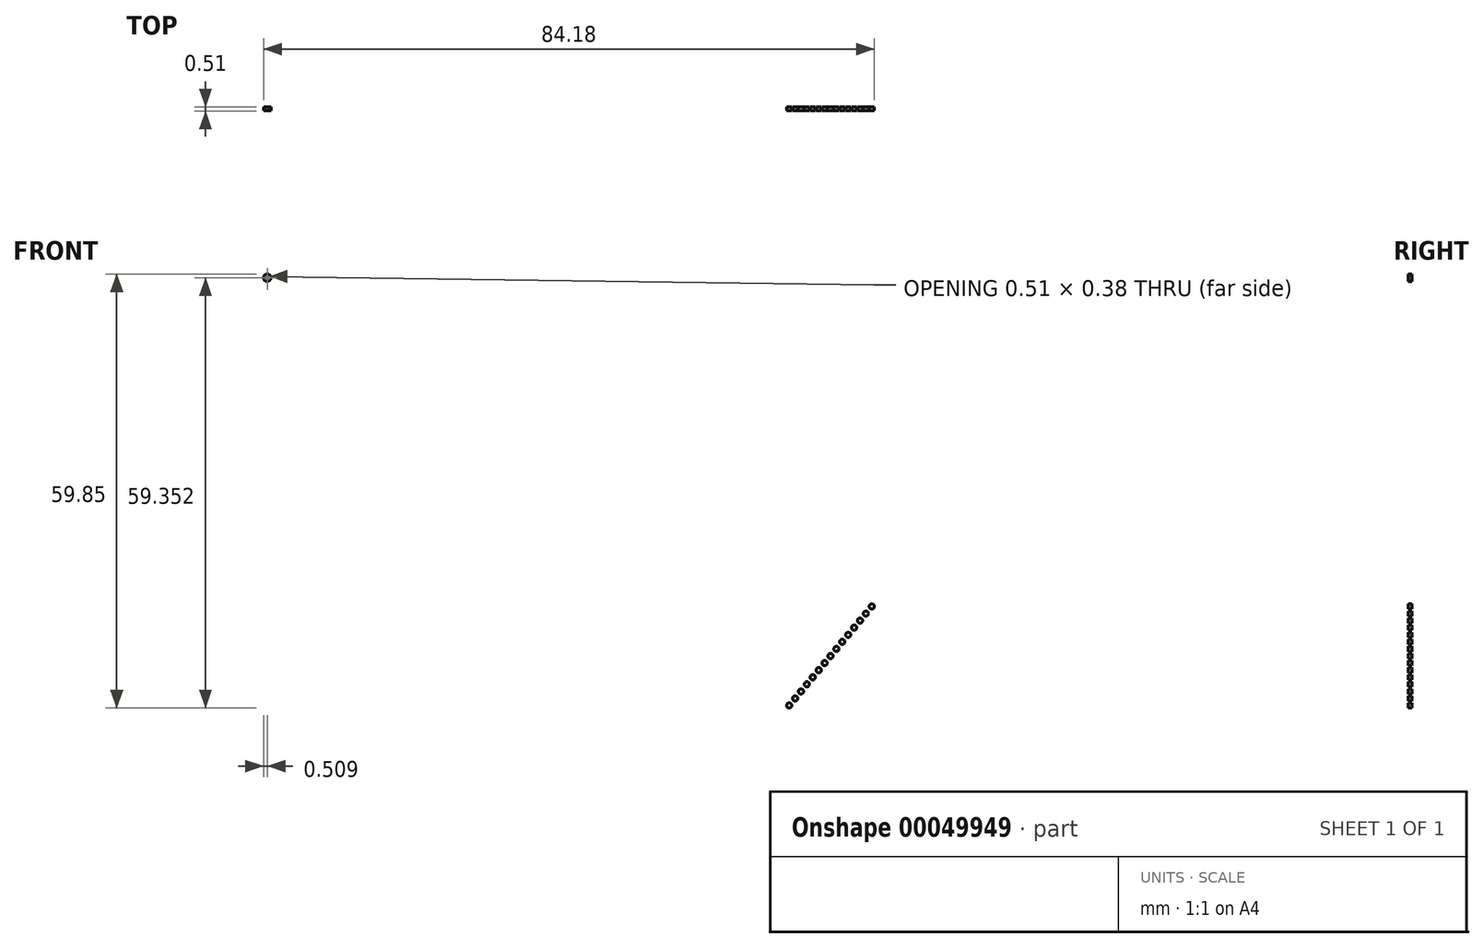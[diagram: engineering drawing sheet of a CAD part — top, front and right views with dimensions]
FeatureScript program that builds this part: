
annotation { "Feature Type Name" : "Feature", "Feature Type Description" : "" }
export const myFeature = defineFeature(function(context is Context, id is Id, definition is map)
    precondition{}
    {
        {
            var Q0;
            Q0=qCreatedBy(makeId("Front.planeOp"),FACE);
            var sketch = newSketch(context, id + "F0", { "sketchPlane" : qUnion([Q0])});
            skCircle(sketch, "E0", {"center": v(-69.08, 60.75) * mm, "radius": 0.5 * mm});
            skLineSegment(sketch, "E1", {"start": v(-69.59, 60.75) * mm, "end": v(-69.59, 55.67) * mm, "construction": true});
            skLineSegment(sketch, "E2", {"start": v(-69.08, 60.24) * mm, "end": v(-74.16, 60.24) * mm, "construction": true});
            skLineSegment(sketch, "E3", {"start": v(-69.33, 60.75) * mm, "end": v(-69.33, 60.57) * mm});
            skLineSegment(sketch, "E4", {"start": v(-68.83, 60.75) * mm, "end": v(-68.83, 60.57) * mm});
            skLineSegment(sketch, "E5", {"start": v(-69.33, 60.75) * mm, "end": v(-69.33, 60.95) * mm});
            skLineSegment(sketch, "E6", {"start": v(-69.33, 60.57) * mm, "end": v(-69.23, 60.57) * mm});
            skLineSegment(sketch, "E7", {"start": v(-69.23, 60.57) * mm, "end": v(-69.23, 60.84) * mm});
            skLineSegment(sketch, "E8", {"start": v(-69.08, 60.75) * mm, "end": v(-69.08, 60.69) * mm});
            skLineSegment(sketch, "E9", {"start": v(-68.83, 60.57) * mm, "end": v(-68.93, 60.57) * mm});
            skLineSegment(sketch, "E10", {"start": v(-68.93, 60.57) * mm, "end": v(-68.93, 60.84) * mm});
            skLineSegment(sketch, "E11", {"start": v(-69.08, 60.75) * mm, "end": v(-69.08, 60.24) * mm});
            skLineSegment(sketch, "E12", {"start": v(-69.08, 60.75) * mm, "end": v(-69.08, 61.26) * mm});
            skLineSegment(sketch, "E13", {"start": v(-69.33, 60.95) * mm, "end": v(-69.23, 60.95) * mm});
            skLineSegment(sketch, "E14", {"start": v(-69.23, 60.95) * mm, "end": v(-69.23, 60.93) * mm});
            skLineSegment(sketch, "E15", {"start": v(-69.08, 60.7) * mm, "end": v(-68.93, 60.7) * mm, "construction": true});
            skLineSegment(sketch, "E16", {"start": v(-69.08, 60.66) * mm, "end": v(-69.23, 60.66) * mm, "construction": true});
            skLineSegment(sketch, "E17", {"start": v(-69.08, 60.75) * mm, "end": v(-69.08, 60.57) * mm});
            skLineSegment(sketch, "E18", {"start": v(-69.08, 60.57) * mm, "end": v(-69.13, 60.57) * mm});
            skLineSegment(sketch, "E19", {"start": v(-69.08, 60.57) * mm, "end": v(-69.03, 60.57) * mm});
            skLineSegment(sketch, "E20", {"start": v(-69.13, 60.57) * mm, "end": v(-69.13, 60.84) * mm});
            skLineSegment(sketch, "E21", {"start": v(-69.03, 60.57) * mm, "end": v(-69.03, 60.84) * mm});
            skLineSegment(sketch, "E22", {"start": v(-69.23, 60.84) * mm, "end": v(-69.13, 60.84) * mm, "construction": true});
            skLineSegment(sketch, "E23", {"start": v(-69.03, 60.84) * mm, "end": v(-68.93, 60.84) * mm, "construction": true});
            skLineSegment(sketch, "E24", {"start": v(-69.18, 60.84) * mm, "end": v(-69.18, 60.86) * mm});
            skLineSegment(sketch, "E25", {"start": v(-68.98, 60.84) * mm, "end": v(-68.98, 60.86) * mm});
            skArc(sketch, "E26", {"start": v(-69.13, 60.84) * mm, "mid": v(-69.18, 60.86) * mm, "end": v(-69.23, 60.84) * mm});
            skArc(sketch, "E27", {"start": v(-68.93, 60.84) * mm, "mid": v(-68.98, 60.86) * mm, "end": v(-69.03, 60.84) * mm});
            skLineSegment(sketch, "E28", {"start": v(-69.23, 60.93) * mm, "end": v(-68.83, 60.93) * mm, "construction": true});
            skLineSegment(sketch, "E29", {"start": v(-69.23, 60.93) * mm, "end": v(-69.08, 60.93) * mm});
            skLineSegment(sketch, "E30", {"start": v(-69.16, 60.93) * mm, "end": v(-69.16, 60.95) * mm});
            skArc(sketch, "E31", {"start": v(-69.08, 60.93) * mm, "mid": v(-69.16, 60.95) * mm, "end": v(-69.23, 60.93) * mm});
            skLineSegment(sketch, "E32", {"start": v(-68.93, 60.84) * mm, "end": v(-68.93, 60.93) * mm, "construction": true});
            skLineSegment(sketch, "E33", {"start": v(-69.08, 60.93) * mm, "end": v(-68.93, 60.93) * mm});
            skLineSegment(sketch, "E34", {"start": v(-69, 60.93) * mm, "end": v(-69, 60.95) * mm});
            skArc(sketch, "E35", {"start": v(-68.93, 60.93) * mm, "mid": v(-69, 60.95) * mm, "end": v(-69.08, 60.93) * mm});
            skLineSegment(sketch, "E36", {"start": v(-68.85, 60.93) * mm, "end": v(-68.83, 60.9) * mm});
            skLineSegment(sketch, "E37", {"start": v(-68.84, 60.91) * mm, "end": v(-68.84, 60.92) * mm});
            skArc(sketch, "E38", {"start": v(-68.83, 60.9) * mm, "mid": v(-68.84, 60.92) * mm, "end": v(-68.85, 60.93) * mm});
            skLineSegment(sketch, "E39", {"start": v(-68.93, 60.93) * mm, "end": v(-68.85, 60.93) * mm});
            skLineSegment(sketch, "E40", {"start": v(-68.83, 60.9) * mm, "end": v(-68.83, 60.75) * mm});
            skLineSegment(sketch, "E41", {"start": v(15.33, 16.73) * mm, "end": v(2.62, 1.49) * mm});
            skCircle(sketch, "E42", {"center": v(2.85, 1.76) * mm, "radius": 0.36 * mm});
            skLineSegment(sketch, "E43", {"start": v(2.85, 1.76) * mm, "end": v(2.58, 1.99) * mm});
            skLineSegment(sketch, "E44", {"start": v(2.58, 1.99) * mm, "end": v(3.4, 2.96) * mm, "construction": true});
            skLineSegment(sketch, "E45", {"start": v(3.4, 2.96) * mm, "end": v(3.67, 2.74) * mm});
            skCircle(sketch, "E46", {"center": v(3.67, 2.74) * mm, "radius": 0.36 * mm});
            skLineSegment(sketch, "E47", {"start": v(3.4, 2.96) * mm, "end": v(4.2, 3.94) * mm, "construction": true});
            skLineSegment(sketch, "E48", {"start": v(4.2, 3.94) * mm, "end": v(4.48, 3.71) * mm});
            skCircle(sketch, "E49", {"center": v(4.48, 3.71) * mm, "radius": 0.36 * mm});
            skLineSegment(sketch, "E50", {"start": v(4.2, 3.94) * mm, "end": v(5.02, 4.92) * mm, "construction": true});
            skLineSegment(sketch, "E51", {"start": v(5.02, 4.92) * mm, "end": v(5.3, 4.69) * mm});
            skCircle(sketch, "E52", {"center": v(5.3, 4.69) * mm, "radius": 0.36 * mm});
            skLineSegment(sketch, "E53", {"start": v(5.02, 4.92) * mm, "end": v(5.83, 5.9) * mm, "construction": true});
            skLineSegment(sketch, "E54", {"start": v(5.83, 5.9) * mm, "end": v(6.1, 5.66) * mm});
            skCircle(sketch, "E55", {"center": v(6.1, 5.66) * mm, "radius": 0.36 * mm});
            skLineSegment(sketch, "E56", {"start": v(5.83, 5.9) * mm, "end": v(6.64, 6.87) * mm, "construction": true});
            skLineSegment(sketch, "E57", {"start": v(6.64, 6.87) * mm, "end": v(6.92, 6.64) * mm});
            skCircle(sketch, "E58", {"center": v(6.92, 6.64) * mm, "radius": 0.36 * mm});
            skLineSegment(sketch, "E59", {"start": v(6.64, 6.87) * mm, "end": v(7.46, 7.84) * mm, "construction": true});
            skLineSegment(sketch, "E60", {"start": v(7.46, 7.84) * mm, "end": v(7.73, 7.61) * mm});
            skCircle(sketch, "E61", {"center": v(7.73, 7.61) * mm, "radius": 0.36 * mm});
            skLineSegment(sketch, "E62", {"start": v(7.46, 7.84) * mm, "end": v(8.27, 8.82) * mm, "construction": true});
            skLineSegment(sketch, "E63", {"start": v(8.27, 8.82) * mm, "end": v(8.54, 8.6) * mm});
            skCircle(sketch, "E64", {"center": v(8.54, 8.6) * mm, "radius": 0.36 * mm});
            skLineSegment(sketch, "E65", {"start": v(8.27, 8.82) * mm, "end": v(9.08, 9.8) * mm, "construction": true});
            skLineSegment(sketch, "E66", {"start": v(9.08, 9.8) * mm, "end": v(9.36, 9.57) * mm});
            skCircle(sketch, "E67", {"center": v(9.36, 9.57) * mm, "radius": 0.36 * mm});
            skLineSegment(sketch, "E68", {"start": v(9.08, 9.8) * mm, "end": v(9.9, 10.77) * mm, "construction": true});
            skLineSegment(sketch, "E69", {"start": v(9.9, 10.77) * mm, "end": v(10.17, 10.54) * mm});
            skCircle(sketch, "E70", {"center": v(10.17, 10.54) * mm, "radius": 0.36 * mm});
            skLineSegment(sketch, "E71", {"start": v(9.9, 10.77) * mm, "end": v(10.7, 11.74) * mm, "construction": true});
            skLineSegment(sketch, "E72", {"start": v(10.7, 11.74) * mm, "end": v(10.98, 11.52) * mm});
            skLineSegment(sketch, "E73", {"start": v(10.7, 11.74) * mm, "end": v(11.52, 12.72) * mm, "construction": true});
            skLineSegment(sketch, "E74", {"start": v(11.52, 12.72) * mm, "end": v(11.8, 12.5) * mm, "construction": true});
            skLineSegment(sketch, "E75", {"start": v(11.52, 12.72) * mm, "end": v(12.34, 13.7) * mm, "construction": true});
            skLineSegment(sketch, "E76", {"start": v(12.34, 13.7) * mm, "end": v(12.6, 13.47) * mm});
            skLineSegment(sketch, "E77", {"start": v(12.34, 13.7) * mm, "end": v(13.15, 14.67) * mm, "construction": true});
            skLineSegment(sketch, "E78", {"start": v(13.15, 14.67) * mm, "end": v(13.42, 14.44) * mm});
            skLineSegment(sketch, "E79", {"start": v(13.15, 14.67) * mm, "end": v(13.96, 15.65) * mm, "construction": true});
            skLineSegment(sketch, "E80", {"start": v(13.96, 15.65) * mm, "end": v(14.23, 15.42) * mm});
            skLineSegment(sketch, "E81", {"start": v(13.96, 15.65) * mm, "end": v(14.77, 16.62) * mm, "construction": true});
            skLineSegment(sketch, "E82", {"start": v(14.77, 16.62) * mm, "end": v(15.05, 16.4) * mm, "construction": true});
            skCircle(sketch, "E83", {"center": v(10.98, 11.52) * mm, "radius": 0.36 * mm});
            skCircle(sketch, "E84", {"center": v(11.8, 12.5) * mm, "radius": 0.36 * mm});
            skCircle(sketch, "E85", {"center": v(13.42, 14.44) * mm, "radius": 0.36 * mm});
            skCircle(sketch, "E86", {"center": v(12.6, 13.47) * mm, "radius": 0.36 * mm});
            skCircle(sketch, "E87", {"center": v(14.23, 15.42) * mm, "radius": 0.36 * mm});
            skCircle(sketch, "E88", {"center": v(15.05, 16.4) * mm, "radius": 0.36 * mm});
            skSolve(sketch);
        }
        {
            var Q0;
            Q0=makeQuery(id+"F0.imprint","IMPRINT",FACE,{"disambiguationData":[TD([[makeQuery(id+"F0.imprint","IMPRINT",EDGE,{"derivedFrom":sQuery(id+"F0.wireOp",EDGE,"E3")}),-1.0]])]});
            var Q1;
            Q1=makeQuery(id+"F0.imprint","IMPRINT",FACE,{"disambiguationData":[TD([[makeQuery(id+"F0.imprint","IMPRINT",EDGE,{"derivedFrom":sQuery(id+"F0.wireOp",EDGE,"E4")}),1.0]])]});
            var Q2;
            {var subQ0=sQuery(id+"F0.wireOp",EDGE,"E41");var subQ1=makeQuery(id+"F0.imprint","INTERSECT",VERTEX,{"derivedFrom":[subQ0,sQuery(id+"F0.wireOp",EDGE,"E72")]});Q2=makeQuery(id+"F0.imprint","IMPRINT",FACE,{"disambiguationData":[TD([[makeQuery(id+"F0.imprint","IMPRINT",EDGE,{"disambiguationData":[TD([[subQ1,1.0]])],"derivedFrom":subQ0}),1.0]])]});}
            var Q3;
            {var subQ0=sQuery(id+"F0.wireOp",EDGE,"E41");var subQ1=makeQuery(id+"F0.imprint","INTERSECT",VERTEX,{"derivedFrom":[subQ0,sQuery(id+"F0.wireOp",EDGE,"E69")]});Q3=makeQuery(id+"F0.imprint","IMPRINT",FACE,{"disambiguationData":[TD([[makeQuery(id+"F0.imprint","IMPRINT",EDGE,{"disambiguationData":[TD([[subQ1,1.0]])],"derivedFrom":subQ0}),1.0]])]});}
            var Q4;
            {var subQ0=sQuery(id+"F0.wireOp",EDGE,"E60");Q4=makeQuery(id+"F0.imprint","IMPRINT",FACE,{"disambiguationData":[TD([[makeQuery(id+"F0.imprint","IMPRINT",EDGE,{"derivedFrom":subQ0}),1.0]])]});}
            var Q5;
            {var subQ0=sQuery(id+"F0.wireOp",EDGE,"E63");Q5=makeQuery(id+"F0.imprint","IMPRINT",FACE,{"disambiguationData":[TD([[makeQuery(id+"F0.imprint","IMPRINT",EDGE,{"derivedFrom":subQ0}),-1.0]])]});}
            var Q6;
            {var subQ0=sQuery(id+"F0.wireOp",EDGE,"E41");var subQ1=makeQuery(id+"F0.imprint","INTERSECT",VERTEX,{"derivedFrom":[subQ0,sQuery(id+"F0.wireOp",EDGE,"E43")]});Q6=makeQuery(id+"F0.imprint","IMPRINT",FACE,{"disambiguationData":[TD([[makeQuery(id+"F0.imprint","IMPRINT",EDGE,{"disambiguationData":[TD([[subQ1,1.0]])],"derivedFrom":subQ0}),1.0]])]});}
            var Q7;
            {var subQ0=sQuery(id+"F0.wireOp",EDGE,"E60");Q7=makeQuery(id+"F0.imprint","IMPRINT",FACE,{"disambiguationData":[TD([[makeQuery(id+"F0.imprint","IMPRINT",EDGE,{"derivedFrom":subQ0}),-1.0]])]});}
            var Q8;
            {var subQ0=sQuery(id+"F0.wireOp",EDGE,"E54");Q8=makeQuery(id+"F0.imprint","IMPRINT",FACE,{"disambiguationData":[TD([[makeQuery(id+"F0.imprint","IMPRINT",EDGE,{"derivedFrom":subQ0}),-1.0]])]});}
            var Q9;
            {var subQ0=sQuery(id+"F0.wireOp",EDGE,"E69");Q9=makeQuery(id+"F0.imprint","IMPRINT",FACE,{"disambiguationData":[TD([[makeQuery(id+"F0.imprint","IMPRINT",EDGE,{"derivedFrom":subQ0}),1.0]])]});}
            var Q10;
            {var subQ0=sQuery(id+"F0.wireOp",EDGE,"E63");Q10=makeQuery(id+"F0.imprint","IMPRINT",FACE,{"disambiguationData":[TD([[makeQuery(id+"F0.imprint","IMPRINT",EDGE,{"derivedFrom":subQ0}),1.0]])]});}
            var Q11;
            {var subQ0=sQuery(id+"F0.wireOp",EDGE,"E48");Q11=makeQuery(id+"F0.imprint","IMPRINT",FACE,{"disambiguationData":[TD([[makeQuery(id+"F0.imprint","IMPRINT",EDGE,{"derivedFrom":subQ0}),-1.0]])]});}
            var Q12;
            {var subQ3=sQuery(id+"F0.wireOp",EDGE,"E43");Q12=makeQuery(id+"F0.imprint","IMPRINT",FACE,{"disambiguationData":[TD([[makeQuery(id+"F0.imprint","IMPRINT",EDGE,{"derivedFrom":subQ3}),1.0]])]});}
            var Q13;
            {var subQ0=sQuery(id+"F0.wireOp",EDGE,"E57");Q13=makeQuery(id+"F0.imprint","IMPRINT",FACE,{"disambiguationData":[TD([[makeQuery(id+"F0.imprint","IMPRINT",EDGE,{"derivedFrom":subQ0}),1.0]])]});}
            var Q14;
            {var subQ0=sQuery(id+"F0.wireOp",EDGE,"E51");Q14=makeQuery(id+"F0.imprint","IMPRINT",FACE,{"disambiguationData":[TD([[makeQuery(id+"F0.imprint","IMPRINT",EDGE,{"derivedFrom":subQ0}),-1.0]])]});}
            var Q15;
            {var subQ0=sQuery(id+"F0.wireOp",EDGE,"E41");var subQ1=makeQuery(id+"F0.imprint","INTERSECT",VERTEX,{"derivedFrom":[subQ0,sQuery(id+"F0.wireOp",EDGE,"E45")]});Q15=makeQuery(id+"F0.imprint","IMPRINT",FACE,{"disambiguationData":[TD([[makeQuery(id+"F0.imprint","IMPRINT",EDGE,{"disambiguationData":[TD([[subQ1,1.0]])],"derivedFrom":subQ0}),1.0]])]});}
            var Q16;
            {var subQ0=sQuery(id+"F0.wireOp",EDGE,"E48");Q16=makeQuery(id+"F0.imprint","IMPRINT",FACE,{"disambiguationData":[TD([[makeQuery(id+"F0.imprint","IMPRINT",EDGE,{"derivedFrom":subQ0}),1.0]])]});}
            var Q17;
            {var subQ0=sQuery(id+"F0.wireOp",EDGE,"E57");Q17=makeQuery(id+"F0.imprint","IMPRINT",FACE,{"disambiguationData":[TD([[makeQuery(id+"F0.imprint","IMPRINT",EDGE,{"derivedFrom":subQ0}),-1.0]])]});}
            var Q18;
            {var subQ0=sQuery(id+"F0.wireOp",EDGE,"E41");var subQ1=makeQuery(id+"F0.imprint","INTERSECT",VERTEX,{"derivedFrom":[subQ0,sQuery(id+"F0.wireOp",EDGE,"E48")]});Q18=makeQuery(id+"F0.imprint","IMPRINT",FACE,{"disambiguationData":[TD([[makeQuery(id+"F0.imprint","IMPRINT",EDGE,{"disambiguationData":[TD([[subQ1,1.0]])],"derivedFrom":subQ0}),1.0]])]});}
            var Q19;
            {var subQ0=sQuery(id+"F0.wireOp",EDGE,"E41");var subQ1=makeQuery(id+"F0.imprint","INTERSECT",VERTEX,{"derivedFrom":[subQ0,sQuery(id+"F0.wireOp",EDGE,"E63")]});Q19=makeQuery(id+"F0.imprint","IMPRINT",FACE,{"disambiguationData":[TD([[makeQuery(id+"F0.imprint","IMPRINT",EDGE,{"disambiguationData":[TD([[subQ1,1.0]])],"derivedFrom":subQ0}),1.0]])]});}
            var Q20;
            {var subQ0=sQuery(id+"F0.wireOp",EDGE,"E72");Q20=makeQuery(id+"F0.imprint","IMPRINT",FACE,{"disambiguationData":[TD([[makeQuery(id+"F0.imprint","IMPRINT",EDGE,{"derivedFrom":subQ0}),1.0]])]});}
            var Q21;
            {var subQ0=sQuery(id+"F0.wireOp",EDGE,"E54");Q21=makeQuery(id+"F0.imprint","IMPRINT",FACE,{"disambiguationData":[TD([[makeQuery(id+"F0.imprint","IMPRINT",EDGE,{"derivedFrom":subQ0}),1.0]])]});}
            var Q22;
            {var subQ0=sQuery(id+"F0.wireOp",EDGE,"E88");var subQ1=sQuery(id+"F0.wireOp",EDGE,"E41");var subQ2=makeQuery(id+"F0.imprint","INTERSECT",VERTEX,{"disambiguationData":[OD(0.0)],"derivedFrom":[subQ1,subQ0]});Q22=makeQuery(id+"F0.imprint","IMPRINT",FACE,{"disambiguationData":[TD([[makeQuery(id+"F0.imprint","IMPRINT",EDGE,{"disambiguationData":[TD([[subQ2,1.0]])],"derivedFrom":subQ1}),-1.0]])]});}
            var Q23;
            {var subQ0=sQuery(id+"F0.wireOp",EDGE,"E88");var subQ1=sQuery(id+"F0.wireOp",EDGE,"E41");var subQ2=makeQuery(id+"F0.imprint","INTERSECT",VERTEX,{"disambiguationData":[OD(0.0)],"derivedFrom":[subQ1,subQ0]});Q23=makeQuery(id+"F0.imprint","IMPRINT",FACE,{"disambiguationData":[TD([[makeQuery(id+"F0.imprint","IMPRINT",EDGE,{"disambiguationData":[TD([[subQ2,1.0]])],"derivedFrom":subQ1}),1.0]])]});}
            var Q24;
            {var subQ0=sQuery(id+"F0.wireOp",EDGE,"E84");var subQ1=sQuery(id+"F0.wireOp",EDGE,"E41");var subQ2=makeQuery(id+"F0.imprint","INTERSECT",VERTEX,{"disambiguationData":[OD(0.0)],"derivedFrom":[subQ1,subQ0]});Q24=makeQuery(id+"F0.imprint","IMPRINT",FACE,{"disambiguationData":[TD([[makeQuery(id+"F0.imprint","IMPRINT",EDGE,{"disambiguationData":[TD([[subQ2,1.0]])],"derivedFrom":subQ1}),-1.0]])]});}
            var Q25;
            {var subQ0=sQuery(id+"F0.wireOp",EDGE,"E84");var subQ1=sQuery(id+"F0.wireOp",EDGE,"E41");var subQ2=makeQuery(id+"F0.imprint","INTERSECT",VERTEX,{"disambiguationData":[OD(0.0)],"derivedFrom":[subQ1,subQ0]});Q25=makeQuery(id+"F0.imprint","IMPRINT",FACE,{"disambiguationData":[TD([[makeQuery(id+"F0.imprint","IMPRINT",EDGE,{"disambiguationData":[TD([[subQ2,1.0]])],"derivedFrom":subQ1}),1.0]])]});}
            var Q26;
            {var subQ0=sQuery(id+"F0.wireOp",EDGE,"E41");var subQ1=makeQuery(id+"F0.imprint","INTERSECT",VERTEX,{"derivedFrom":[subQ0,sQuery(id+"F0.wireOp",EDGE,"E80")]});Q26=makeQuery(id+"F0.imprint","IMPRINT",FACE,{"disambiguationData":[TD([[makeQuery(id+"F0.imprint","IMPRINT",EDGE,{"disambiguationData":[TD([[subQ1,1.0]])],"derivedFrom":subQ0}),1.0]])]});}
            var Q27;
            {var subQ0=sQuery(id+"F0.wireOp",EDGE,"E80");Q27=makeQuery(id+"F0.imprint","IMPRINT",FACE,{"disambiguationData":[TD([[makeQuery(id+"F0.imprint","IMPRINT",EDGE,{"derivedFrom":subQ0}),-1.0]])]});}
            var Q28;
            {var subQ0=sQuery(id+"F0.wireOp",EDGE,"E41");var subQ1=makeQuery(id+"F0.imprint","INTERSECT",VERTEX,{"derivedFrom":[subQ0,sQuery(id+"F0.wireOp",EDGE,"E78")]});Q28=makeQuery(id+"F0.imprint","IMPRINT",FACE,{"disambiguationData":[TD([[makeQuery(id+"F0.imprint","IMPRINT",EDGE,{"disambiguationData":[TD([[subQ1,1.0]])],"derivedFrom":subQ0}),1.0]])]});}
            var Q29;
            {var subQ0=sQuery(id+"F0.wireOp",EDGE,"E78");Q29=makeQuery(id+"F0.imprint","IMPRINT",FACE,{"disambiguationData":[TD([[makeQuery(id+"F0.imprint","IMPRINT",EDGE,{"derivedFrom":subQ0}),1.0]])]});}
            var Q30;
            {var subQ0=sQuery(id+"F0.wireOp",EDGE,"E41");var subQ1=makeQuery(id+"F0.imprint","INTERSECT",VERTEX,{"derivedFrom":[subQ0,sQuery(id+"F0.wireOp",EDGE,"E76")]});Q30=makeQuery(id+"F0.imprint","IMPRINT",FACE,{"disambiguationData":[TD([[makeQuery(id+"F0.imprint","IMPRINT",EDGE,{"disambiguationData":[TD([[subQ1,1.0]])],"derivedFrom":subQ0}),1.0]])]});}
            var Q31;
            {var subQ0=sQuery(id+"F0.wireOp",EDGE,"E78");Q31=makeQuery(id+"F0.imprint","IMPRINT",FACE,{"disambiguationData":[TD([[makeQuery(id+"F0.imprint","IMPRINT",EDGE,{"derivedFrom":subQ0}),-1.0]])]});}
            var Q32;
            {var subQ0=sQuery(id+"F0.wireOp",EDGE,"E41");var subQ1=makeQuery(id+"F0.imprint","INTERSECT",VERTEX,{"derivedFrom":[subQ0,sQuery(id+"F0.wireOp",EDGE,"E57")]});Q32=makeQuery(id+"F0.imprint","IMPRINT",FACE,{"disambiguationData":[TD([[makeQuery(id+"F0.imprint","IMPRINT",EDGE,{"disambiguationData":[TD([[subQ1,1.0]])],"derivedFrom":subQ0}),1.0]])]});}
            var Q33;
            {var subQ0=sQuery(id+"F0.wireOp",EDGE,"E43");Q33=makeQuery(id+"F0.imprint","IMPRINT",FACE,{"disambiguationData":[TD([[makeQuery(id+"F0.imprint","IMPRINT",EDGE,{"derivedFrom":subQ0}),-1.0]])]});}
            var Q34;
            {var subQ0=sQuery(id+"F0.wireOp",EDGE,"E76");Q34=makeQuery(id+"F0.imprint","IMPRINT",FACE,{"disambiguationData":[TD([[makeQuery(id+"F0.imprint","IMPRINT",EDGE,{"derivedFrom":subQ0}),1.0]])]});}
            var Q35;
            {var subQ0=sQuery(id+"F0.wireOp",EDGE,"E69");Q35=makeQuery(id+"F0.imprint","IMPRINT",FACE,{"disambiguationData":[TD([[makeQuery(id+"F0.imprint","IMPRINT",EDGE,{"derivedFrom":subQ0}),-1.0]])]});}
            var Q36;
            {var subQ0=sQuery(id+"F0.wireOp",EDGE,"E41");var subQ1=makeQuery(id+"F0.imprint","INTERSECT",VERTEX,{"derivedFrom":[subQ0,sQuery(id+"F0.wireOp",EDGE,"E51")]});Q36=makeQuery(id+"F0.imprint","IMPRINT",FACE,{"disambiguationData":[TD([[makeQuery(id+"F0.imprint","IMPRINT",EDGE,{"disambiguationData":[TD([[subQ1,1.0]])],"derivedFrom":subQ0}),1.0]])]});}
            var Q37;
            {var subQ0=sQuery(id+"F0.wireOp",EDGE,"E41");var subQ1=makeQuery(id+"F0.imprint","INTERSECT",VERTEX,{"derivedFrom":[subQ0,sQuery(id+"F0.wireOp",EDGE,"E54")]});Q37=makeQuery(id+"F0.imprint","IMPRINT",FACE,{"disambiguationData":[TD([[makeQuery(id+"F0.imprint","IMPRINT",EDGE,{"disambiguationData":[TD([[subQ1,1.0]])],"derivedFrom":subQ0}),1.0]])]});}
            var Q38;
            {var subQ0=sQuery(id+"F0.wireOp",EDGE,"E45");Q38=makeQuery(id+"F0.imprint","IMPRINT",FACE,{"disambiguationData":[TD([[makeQuery(id+"F0.imprint","IMPRINT",EDGE,{"derivedFrom":subQ0}),1.0]])]});}
            var Q39;
            {var subQ0=sQuery(id+"F0.wireOp",EDGE,"E41");var subQ1=makeQuery(id+"F0.imprint","INTERSECT",VERTEX,{"derivedFrom":[subQ0,sQuery(id+"F0.wireOp",EDGE,"E60")]});Q39=makeQuery(id+"F0.imprint","IMPRINT",FACE,{"disambiguationData":[TD([[makeQuery(id+"F0.imprint","IMPRINT",EDGE,{"disambiguationData":[TD([[subQ1,1.0]])],"derivedFrom":subQ0}),1.0]])]});}
            var Q40;
            {var subQ0=sQuery(id+"F0.wireOp",EDGE,"E45");Q40=makeQuery(id+"F0.imprint","IMPRINT",FACE,{"disambiguationData":[TD([[makeQuery(id+"F0.imprint","IMPRINT",EDGE,{"derivedFrom":subQ0}),-1.0]])]});}
            var Q41;
            {var subQ0=sQuery(id+"F0.wireOp",EDGE,"E41");var subQ1=makeQuery(id+"F0.imprint","INTERSECT",VERTEX,{"derivedFrom":[subQ0,sQuery(id+"F0.wireOp",EDGE,"E66")]});Q41=makeQuery(id+"F0.imprint","IMPRINT",FACE,{"disambiguationData":[TD([[makeQuery(id+"F0.imprint","IMPRINT",EDGE,{"disambiguationData":[TD([[subQ1,1.0]])],"derivedFrom":subQ0}),1.0]])]});}
            var Q42;
            {var subQ0=sQuery(id+"F0.wireOp",EDGE,"E66");Q42=makeQuery(id+"F0.imprint","IMPRINT",FACE,{"disambiguationData":[TD([[makeQuery(id+"F0.imprint","IMPRINT",EDGE,{"derivedFrom":subQ0}),-1.0]])]});}
            var Q43;
            {var subQ0=sQuery(id+"F0.wireOp",EDGE,"E72");Q43=makeQuery(id+"F0.imprint","IMPRINT",FACE,{"disambiguationData":[TD([[makeQuery(id+"F0.imprint","IMPRINT",EDGE,{"derivedFrom":subQ0}),-1.0]])]});}
            var Q44;
            {var subQ0=sQuery(id+"F0.wireOp",EDGE,"E80");Q44=makeQuery(id+"F0.imprint","IMPRINT",FACE,{"disambiguationData":[TD([[makeQuery(id+"F0.imprint","IMPRINT",EDGE,{"derivedFrom":subQ0}),1.0]])]});}
            var Q45;
            {var subQ0=sQuery(id+"F0.wireOp",EDGE,"E76");Q45=makeQuery(id+"F0.imprint","IMPRINT",FACE,{"disambiguationData":[TD([[makeQuery(id+"F0.imprint","IMPRINT",EDGE,{"derivedFrom":subQ0}),-1.0]])]});}
            var Q46;
            {var subQ0=sQuery(id+"F0.wireOp",EDGE,"E66");Q46=makeQuery(id+"F0.imprint","IMPRINT",FACE,{"disambiguationData":[TD([[makeQuery(id+"F0.imprint","IMPRINT",EDGE,{"derivedFrom":subQ0}),1.0]])]});}
            var Q47;
            {var subQ0=sQuery(id+"F0.wireOp",EDGE,"E51");Q47=makeQuery(id+"F0.imprint","IMPRINT",FACE,{"disambiguationData":[TD([[makeQuery(id+"F0.imprint","IMPRINT",EDGE,{"derivedFrom":subQ0}),1.0]])]});}
            extrude(context, id + "F1", {"entities" : qUnion([Q0, Q1, Q2, Q3, Q4, Q5, Q6, Q7, Q8, Q9, Q10, Q11, Q12, Q13, Q14, Q15, Q16, Q17, Q18, Q19, Q20, Q21, Q22, Q23, Q24, Q25, Q26, Q27, Q28, Q29, Q30, Q31, Q32, Q33, Q34, Q35, Q36, Q37, Q38, Q39, Q40, Q41, Q42, Q43, Q44, Q45, Q46, Q47]), "depth" : 0.5 * mm});
        }
    });
